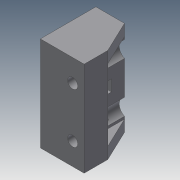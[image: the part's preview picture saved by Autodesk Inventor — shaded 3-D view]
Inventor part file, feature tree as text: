
AUTODESK INVENTOR PART (.ipt)
format: ipt  version: 2020.3 (Build 243373000, 373)  size: 206,336 bytes
history: native  units: in
note: dims shown in document units (in); Inventor stores cm internally (conversion verified against a paired STEP export)
features: sketch x7, extrude x6, hole x2, projected_geometry x2, fillet x1
ambient origin geometry x8: Origin, YZ Plane, XZ Plane, XY Plane, X Axis, Y Axis, Z Axis, Center Point
bodies: Body1 (feature_tree)
feature tree (18):
  extrude  "Extrusion3"  Depth=1.65in TaperAngle=0.0deg
  hole  "Hole1"  [1 undecoded]
  extrude  "Extrusion4"  Depth=0.5in
  hole  "Hole2"  [1 undecoded]
  extrude  "Extrusion5"  Depth=0.45in
  extrude  "Extrusion6"  Depth=0.198in
  extrude  "Extrusion7"  Depth=0.45in
  extrude  "Extrusion8"  Depth=0.5in TaperAngle=0.0deg
  fillet  "Fillet2"  Radius=0.36in
  sketch  "Sketch1"  dims[d10=0.4125in d15=1.65in d16=0.0in]
  projected_geometry  "Projected Loop1"
  sketch  "Sketch3"  dims[d20=0.177in d21=0.75in d22=0.315in d23=0.5575in d24=0.5635in d25=1.0in d26=0.8108in d27=0.2in d28=0.0in]
  sketch  "Sketch4"  dims[d36=0.97in d37=0.5in]
  sketch  "Sketch5"  dims[d38=0.765in d39=0.45in]
  sketch  "Sketch6"  dims[d40=0.45in d41=0.25in]
  sketch  "Sketch7"  dims[d42=0.1in d43=0.75in d44=0.172in d45=0.25in d46=0.6871in d47=0.43in d48=0.8108in d49=0.198in]
  sketch  "Sketch8"  dims[d50=0.072in d51=0.45in d52=0.4in d53=0.0in d54=0.36in d55=0.0in d58=0.3in d59=0.45in d60=0.2in d61=0.0in d63=0.5in d64=0.46in d65=15.0deg d66=0.25in d67=0.0in d68=0.0in d69=0.15in d70=0.15in d71=0.0in d72=0.125in d73=0.875in d74=0.4375in d75=0.565in]
  projected_geometry  "Projected Loop2"
note: 2 required parameter values undecoded (feature->parameter linkage not recoverable at this tier; creation-order binding heuristic only, values carry confidence <= 0.55)
